# Revit family: IS_Synergy_Multiproduct_BIM_BE_L6220;L6221;L6222;L6223;L6224;L6225;L6226;L6227
name_source: partatom
category: Plumbing Fixtures
revit_build: Autodesk Revit 2015 (Build: 20140606_1530(x64)
units: mm (PartAtom-declared; Revit-internal decimal feet)

## types (8) — shared parameters
Assembly Code = C1030200
Default Elevation = 1219 mm
Douchebak = No
DuurEenheid = jaar
FrameMatl = ISI_IdealStandard_Shower_BrightSilver_Render
GlazingMatl = ISI_IdealStandard_Shower_Glass_Render
URL = www.idealstandard.be
Uniclass2 = Pr_40_20_06_79
Urlproducent = www.idealstandard.be
Versie = 1
Volumeunits = liter
zero-valued in all types: Breedte, BrutoGewicht, Diepte, GrootteAfvoergat, Lengte, Vervangingskosten

## per-type parameters (varying)
| type | Accesoires | Afwerking | Auteur | Barcode | Beschrijvingdouchekop | Beschrijvinggarantie | Description | Eigenschappen | Garantieonderdelen | Installatieinstructies | Kleur | Materiaal | Merk | Model | Nettogewicht | NominalDepthActual | Productinformatie | Telefoonnummer | Typeconnectie | Verwachtelevensduur |
| L6220EO - Synergy wet room panel 700 mm |  |  |  |  |  |  | Synergy 700 mm wet room panel |  |  |  |  |  |  | L6220EO | 0 | 700 mm |  |  |  |  |
| L6221EO - Synergy wet room panel 760 mm |  |  |  |  |  |  | Synergy 760 mm wet room panel |  |  |  |  |  |  | L6221EO | 0 | 760 mm |  |  |  |  |
| L6222EO - Synergy wet room panel 800 mm |  |  |  |  |  |  | Synergy 800 mm wet room panel |  |  |  |  |  |  | L6222EO | 0 | 800 mm  [stored 2.62467 ft] |  |  |  |  |
| L6223EO - Synergy wet room panel 900 mm |  |  |  |  |  |  | Synergy 900 mm wet room panel |  |  |  |  |  |  | L6223EO | 0 | 900 mm |  |  |  |  |
| L6224EO - Synergy wet room panel 1000 mm |  |  |  |  |  |  | Synergy 1000 mm wet room panel |  |  |  |  |  |  | L6224EO | 0 | 900 mm |  |  |  |  |
| L6225EO - Synergy wet room panel 1200 mm |  |  |  |  |  |  | Synergy 1200 mm wet room panel |  |  |  |  |  |  | L6225EO | 0 | 900 mm |  |  |  |  |
| L6226EO - Synergy wet room panel 1400 mm |  |  |  |  |  |  | Synergy 1400 mm wet room panel |  |  |  |  |  |  | L6226EO | 0 | 900 mm |  |  |  |  |
| L6227EO - Synergy wet room panel 1600 mm | www.idealstandard.be | Zilverkleurig aluminium | Ideal Standard Produktions-GmbH | 5017830417095 | 0 | Fabrieksgarantie | Synergy 1600 mm wet room panel | Glazen douchepaneel 1600mm van 8 mm transparant veiligheidsglas,
behandeld met Ideal Clean. Met aluminium muurprofiel zilverkleurig. | 2 | www.idealstandard.be | Aluminium zilverkleurig | Veiligheidsglas | Ideal Standard | L6227EO | 57.7 | 900 mm | www.idealstandard.be | 0032 2 325 66 00 | Sanitair | 25 jaar |

note: [stored X ft] marks values corroborated as IEEE doubles in the binary element streams (Revit-internal decimal feet)

## geometry (parser evidence)
native form markers: Blend x6, Sweep x2
no freeform markers — native parametric forms only
